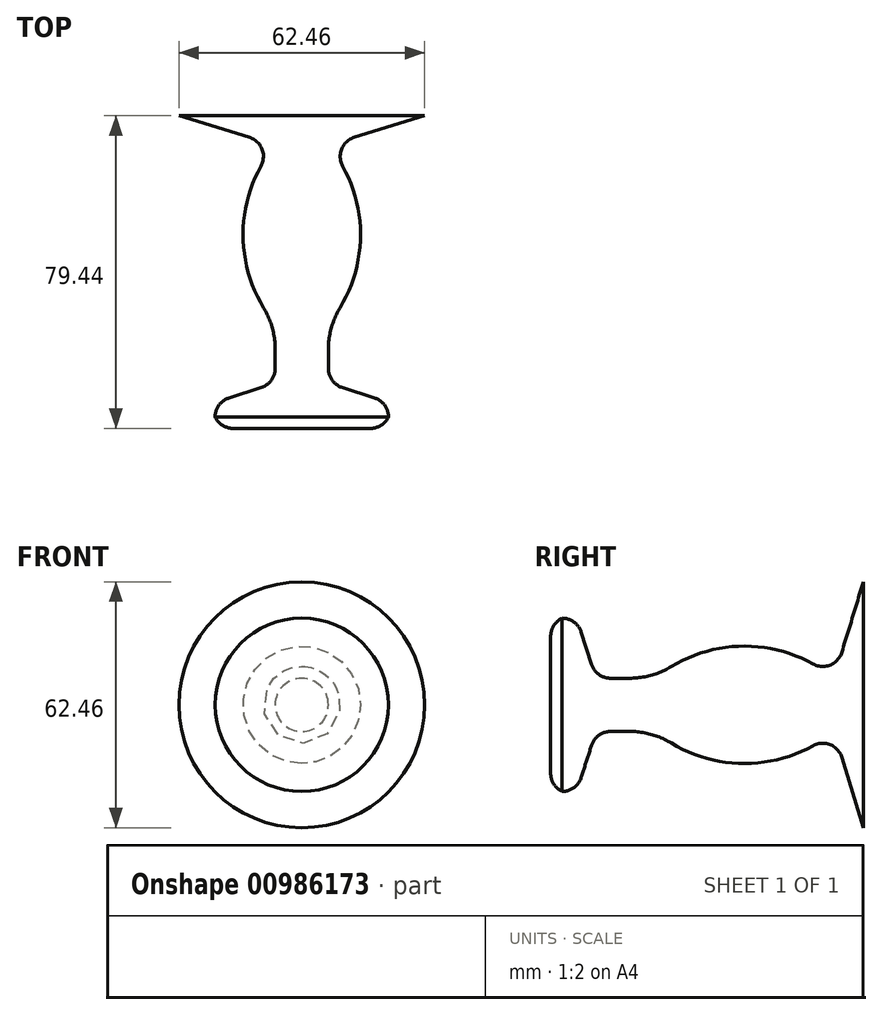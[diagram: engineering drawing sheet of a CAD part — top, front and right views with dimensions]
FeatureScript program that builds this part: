
annotation { "Feature Type Name" : "Feature", "Feature Type Description" : "" }
export const myFeature = defineFeature(function(context is Context, id is Id, definition is map)
    precondition{}
    {
        {
            var Q0;
            Q0=qCreatedBy(makeId("Top.planeOp"),FACE);
            var sketch = newSketch(context, id + "F0", { "sketchPlane" : qUnion([Q0])});
            skLineSegment(sketch, "E0", {"start": v(0, -37.85) * mm, "end": v(22.02, -37.85) * mm});
            skLineSegment(sketch, "E1", {"start": v(22.02, -37.85) * mm, "end": v(22.02, -31.23) * mm});
            skLineSegment(sketch, "E2", {"start": v(22.02, -31.23) * mm, "end": v(6.76, -26.33) * mm});
            skLineSegment(sketch, "E3", {"start": v(6.76, -26.33) * mm, "end": v(6.76, -11.37) * mm});
            skArc(sketch, "E4", {"start": v(6.76, -11.37) * mm, "mid": v(14.92, 11.37) * mm, "end": v(6.76, 34.1) * mm});
            skLineSegment(sketch, "E5", {"start": v(6.76, 34.1) * mm, "end": v(31.23, 41.59) * mm});
            skLineSegment(sketch, "E6", {"start": v(31.23, 41.59) * mm, "end": v(0, 41.59) * mm});
            skLineSegment(sketch, "E7", {"start": v(0, 41.59) * mm, "end": v(0, -37.85) * mm});
            skSolve(sketch);
        }
        {
            var Q0;
            Q0=makeQuery(id+"F0.imprint","IMPRINT",FACE,{"disambiguationData":[TD([[makeQuery(id+"F0.imprint","IMPRINT",EDGE,{"derivedFrom":sQuery(id+"F0.wireOp",EDGE,"E0")}),1.0]])]});
            var Q1;
            Q1=sQuery(id+"F0.wireOp",EDGE,"E7");
            revolve(context, id + "F1", {"surfaceOperationType" : NewSurfaceOperationType.NEW, "entities" : qUnion([Q0]), "axis" : qUnion([Q1]), "revolveType" : RevolveType.FULL});
        }
        {
            var Q0;
            Q0=makeQuery(id+"F1.opRevolve","SWEPT_EDGE",EDGE,{"disambiguationData":[OSD([sQuery(id+"F0.wireOp",EDGE,"E1"),sQuery(id+"F0.wireOp",EDGE,"E2")])]});
            fillet(context, id + "F2", {"entities" : qUnion([Q0]), "radius" : 5.08 * mm, "tangentPropagation" : true, "allowEdgeOverflow" : false});
        }
        {
            var Q0;
            Q0=makeQuery(id+"F1.opRevolve","SWEPT_EDGE",EDGE,{"disambiguationData":[OSD([sQuery(id+"F0.wireOp",EDGE,"E4"),sQuery(id+"F0.wireOp",EDGE,"E5")])]});
            fillet(context, id + "F3", {"entities" : qUnion([Q0]), "radius" : 5.08 * mm, "tangentPropagation" : true, "allowEdgeOverflow" : false});
        }
        {
            var Q0;
            Q0=makeQuery(id+"F1.opRevolve","SWEPT_EDGE",EDGE,{"disambiguationData":[OSD([sQuery(id+"F0.wireOp",EDGE,"E0"),sQuery(id+"F0.wireOp",EDGE,"E1")])]});
            fillet(context, id + "F4", {"entities" : qUnion([Q0]), "radius" : 5.08 * mm, "tangentPropagation" : true, "allowEdgeOverflow" : false});
        }
        {
            var Q0;
            Q0=makeQuery(id+"F1.opRevolve","SWEPT_EDGE",EDGE,{"disambiguationData":[OSD([sQuery(id+"F0.wireOp",EDGE,"E3"),sQuery(id+"F0.wireOp",EDGE,"E4")])]});
            fillet(context, id + "F5", {"entities" : qUnion([Q0]), "radius" : 20.32 * mm, "tangentPropagation" : true, "allowEdgeOverflow" : false});
        }
        {
            var Q0;
            Q0=makeQuery(id+"F1.opRevolve","SWEPT_EDGE",EDGE,{"disambiguationData":[OSD([sQuery(id+"F0.wireOp",EDGE,"E2"),sQuery(id+"F0.wireOp",EDGE,"E3")])]});
            fillet(context, id + "F6", {"entities" : qUnion([Q0]), "radius" : 5.08 * mm, "tangentPropagation" : true, "allowEdgeOverflow" : false});
        }
    });
